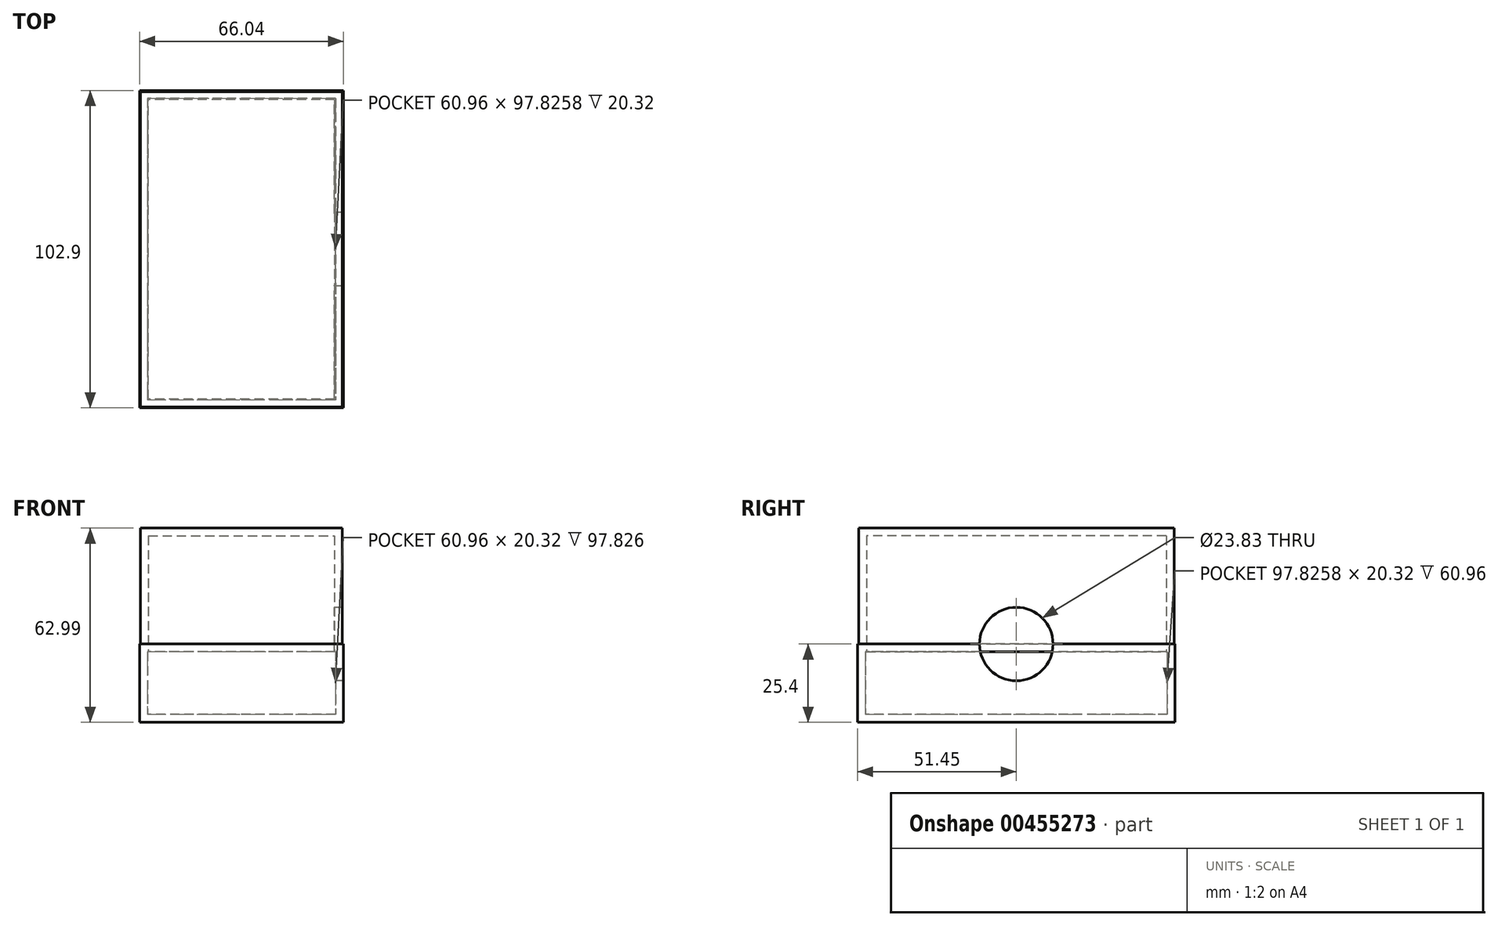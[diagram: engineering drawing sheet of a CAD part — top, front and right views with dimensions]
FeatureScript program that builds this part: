
annotation { "Feature Type Name" : "Feature", "Feature Type Description" : "" }
export const myFeature = defineFeature(function(context is Context, id is Id, definition is map)
    precondition{}
    {
        {
            var Q0;
            Q0=qCreatedBy(makeId("Top.planeOp"),FACE);
            var sketch = newSketch(context, id + "F0", { "sketchPlane" : qUnion([Q0])});
            skLineSegment(sketch, "E0.bottom", {"start": v(33.02, 51.45) * mm, "end": v(-33.02, 51.45) * mm});
            skLineSegment(sketch, "E0.top", {"start": v(33.02, -51.45) * mm, "end": v(-33.02, -51.45) * mm});
            skLineSegment(sketch, "E0.left", {"start": v(33.02, 51.45) * mm, "end": v(33.02, -51.45) * mm});
            skLineSegment(sketch, "E0.right", {"start": v(-33.02, 51.45) * mm, "end": v(-33.02, -51.45) * mm});
            skPoint(sketch, "E0.middle", {"position": v(0, 0) * mm});
            skSolve(sketch);
        }
        {
            var Q0;
            Q0 = qSketchRegion(id + "F0", true);
            extrude(context, id + "F1", {"entities" : qUnion([Q0]), "depth" : 25.4 * mm});
        }
        {
            var Q0;
            Q0=makeQuery(id+"F1.opExtrude","CAP_FACE",FACE,{"disambiguationData":[OSD([sQuery(id+"F0.wireOp",EDGE,"E0.bottom"),sQuery(id+"F0.wireOp",EDGE,"E0.top"),sQuery(id+"F0.wireOp",EDGE,"E0.left"),sQuery(id+"F0.wireOp",EDGE,"E0.right")])],"isStart":false});
            shell(context, id + "F2", {"entities" : qUnion([Q0]), "thickness" : 2.54 * mm});
        }
        {
            var Q0;
            Q0=qCreatedBy(makeId("Top.planeOp"),FACE);
            var sketch = newSketch(context, id + "F3", { "sketchPlane" : qUnion([Q0])});
            skLineSegment(sketch, "E1.bottom", {"start": v(-32.71, 51.11) * mm, "end": v(32.71, 51.11) * mm});
            skLineSegment(sketch, "E1.top", {"start": v(-32.71, -51.11) * mm, "end": v(32.71, -51.11) * mm});
            skLineSegment(sketch, "E1.left", {"start": v(-32.71, 51.11) * mm, "end": v(-32.71, -51.11) * mm});
            skLineSegment(sketch, "E1.right", {"start": v(32.71, 51.11) * mm, "end": v(32.71, -51.11) * mm});
            skPoint(sketch, "E1.middle", {"position": v(0, 0) * mm});
            skSolve(sketch);
        }
        {
            var Q0;
            Q0 = qSketchRegion(id + "F3", true);
            extrude(context, id + "F4", {"entities" : qUnion([Q0]), "operationType" : NewBodyOperationType.ADD, "depth" : 63 * mm});
        }
        {
            var Q0;
            Q0=makeQuery(id+"F4.opExtrude","SWEPT_FACE",FACE,{"disambiguationData":[OSD([sQuery(id+"F3.wireOp",EDGE,"E1.right")])]});
            var sketch = newSketch(context, id + "F5", { "sketchPlane" : qUnion([Q0])});
            skCircle(sketch, "E2", {"center": v(0, 25.4) * mm, "radius": 11.92 * mm});
            skSolve(sketch);
        }
        {
            var Q0;
            Q0 = qSketchRegion(id + "F5", true);
            extrude(context, id + "F6", {"entities" : qUnion([Q0]), "operationType" : NewBodyOperationType.ADD, "depth" : 25.4 * mm});
        }
        {
            var Q0;
            Q0=makeQuery(id+"F6.opExtrude","CAP_FACE",FACE,{"disambiguationData":[OSD([sQuery(id+"F5.wireOp",EDGE,"E2")])],"isStart":false});
            var Q1;
            Q1=makeQuery(id+"F6.opExtrude","SWEPT_FACE",FACE,{"disambiguationData":[OSD([sQuery(id+"F5.wireOp",EDGE,"E2")])]});
            shell(context, id + "F7", {"entities" : qUnion([Q0, Q1]), "thickness" : 2.54 * mm});
        }
    });
